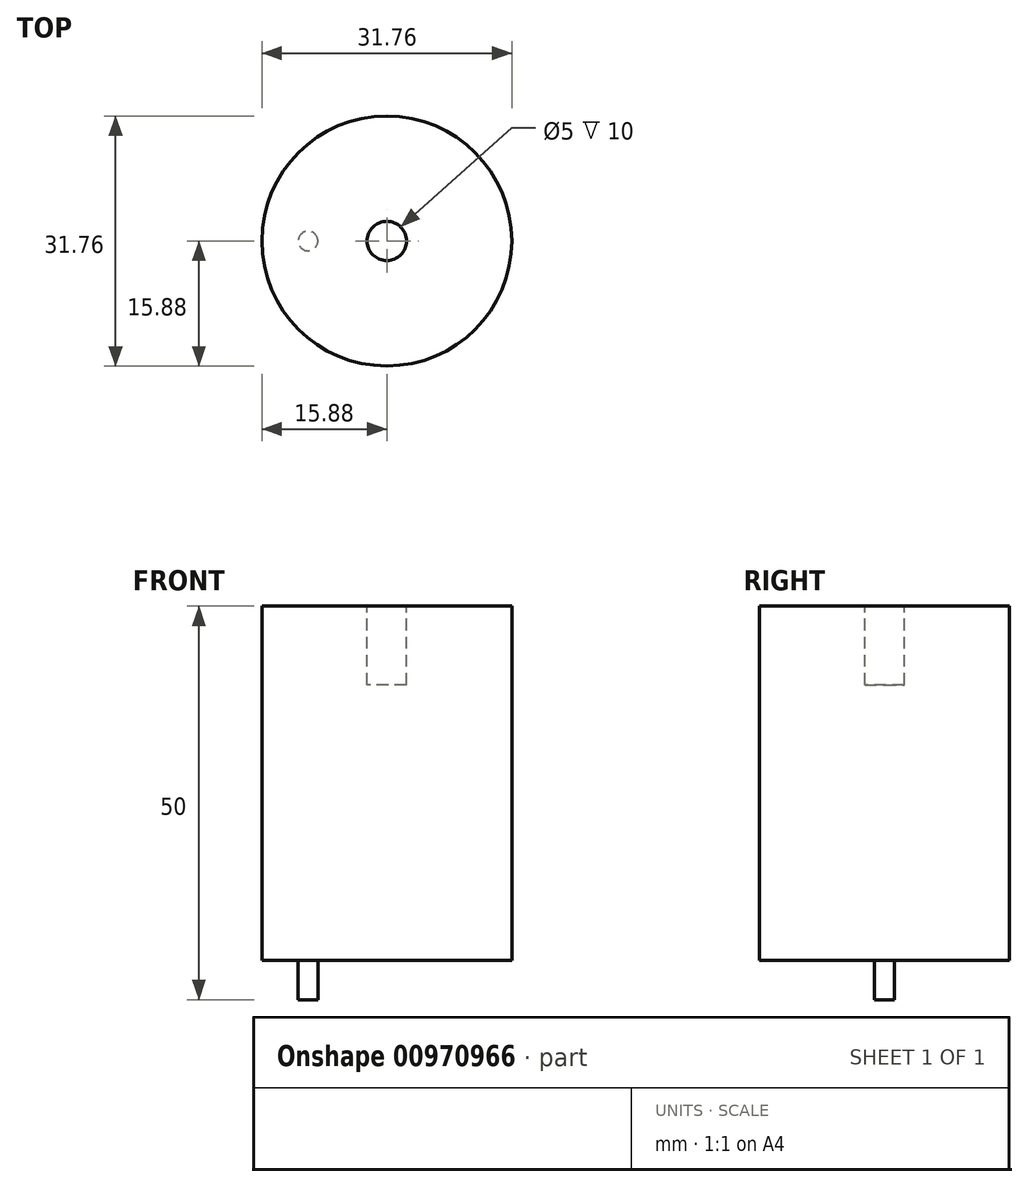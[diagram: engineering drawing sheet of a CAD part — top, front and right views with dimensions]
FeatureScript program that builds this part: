
annotation { "Feature Type Name" : "Feature", "Feature Type Description" : "" }
export const myFeature = defineFeature(function(context is Context, id is Id, definition is map)
    precondition{}
    {
        {
            var Q0;
            Q0=qCreatedBy(makeId("Top.planeOp"),FACE);
            var sketch = newSketch(context, id + "F0", { "sketchPlane" : qUnion([Q0])});
            skCircle(sketch, "E0", {"center": v(0, 0) * mm, "radius": 15.87 * mm});
            skSolve(sketch);
        }
        {
            var Q0;
            Q0=makeQuery(id+"F0.imprint","IMPRINT",FACE,{"disambiguationData":[TD([[makeQuery(id+"F0.imprint","IMPRINT",EDGE,{"derivedFrom":sQuery(id+"F0.wireOp",EDGE,"E0")}),1.0]])]});
            extrude(context, id + "F1", {"entities" : qUnion([Q0]), "depth" : 50 * mm, "offsetDistance" : 25 * mm});
        }
        {
            var Q0;
            Q0=makeQuery(id+"F1.opExtrude","CAP_FACE",FACE,{"disambiguationData":[OSD([sQuery(id+"F0.wireOp",EDGE,"E0")])],"isStart":false});
            var sketch = newSketch(context, id + "F2", { "sketchPlane" : qUnion([Q0])});
            skCircle(sketch, "E1", {"center": v(0, 0) * mm, "radius": 2.5 * mm});
            skSolve(sketch);
        }
        {
            var Q0;
            Q0=makeQuery(id+"F2.imprint","IMPRINT",FACE,{"disambiguationData":[TD([[makeQuery(id+"F2.imprint","IMPRINT",EDGE,{"derivedFrom":sQuery(id+"F2.wireOp",EDGE,"E1")}),1.0]])]});
            extrude(context, id + "F3", {"entities" : qUnion([Q0]), "operationType" : NewBodyOperationType.REMOVE, "oppositeDirection" : true, "depth" : 10 * mm, "offsetDistance" : 25 * mm});
        }
        {
            var Q0;
            Q0=makeQuery(id+"F1.opExtrude","CAP_FACE",FACE,{"disambiguationData":[OSD([sQuery(id+"F0.wireOp",EDGE,"E0")])],"isStart":true});
            var sketch = newSketch(context, id + "F4", { "sketchPlane" : qUnion([Q0])});
            skCircle(sketch, "E2", {"center": v(10, 0) * mm, "radius": 1.25 * mm});
            skCircle(sketch, "E3.MirrorC", {"center": v(-10, 0) * mm, "radius": 1.25 * mm});
            skSolve(sketch);
        }
        {
            var Q0;
            Q0=makeQuery(id+"F4.imprint","IMPRINT",FACE,{"disambiguationData":[TD([[makeQuery(id+"F4.imprint","IMPRINT",EDGE,{"derivedFrom":sQuery(id+"F4.wireOp",EDGE,"E2")}),1.0]])]});
            var Q1;
            Q1=makeQuery(id+"F4.imprint","IMPRINT",FACE,{"disambiguationData":[TD([[makeQuery(id+"F4.imprint","IMPRINT",EDGE,{"derivedFrom":sQuery(id+"F4.wireOp",EDGE,"E3.MirrorC")}),-1.0]])]});
            extrude(context, id + "F5", {"entities" : qUnion([Q0, Q1]), "operationType" : NewBodyOperationType.REMOVE, "oppositeDirection" : true, "depth" : 5 * mm, "offsetDistance" : 25 * mm});
        }
    });
